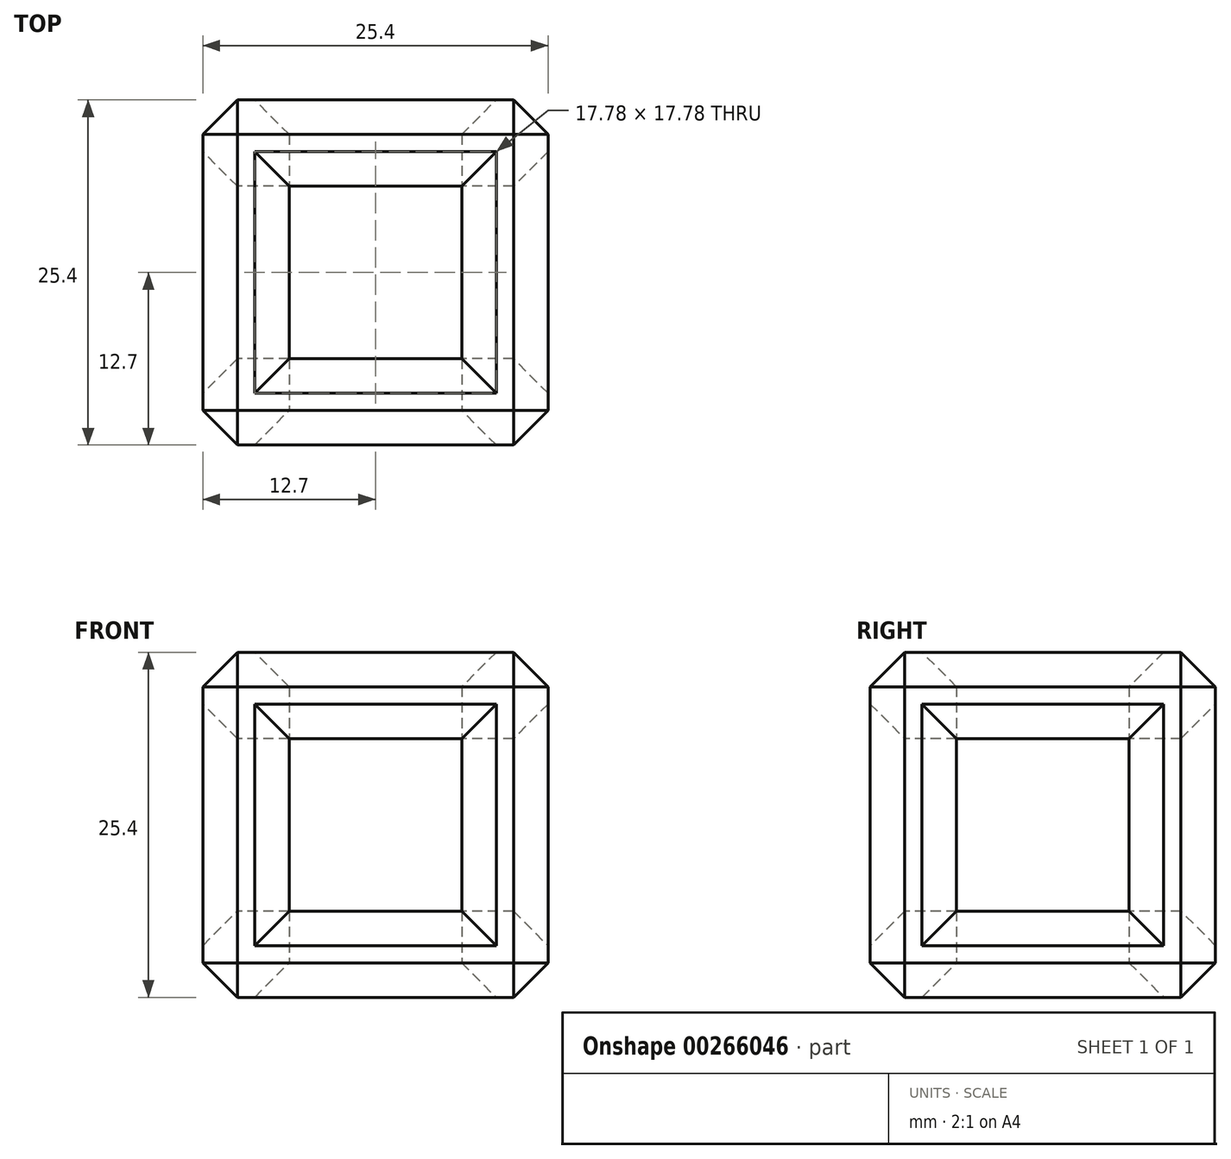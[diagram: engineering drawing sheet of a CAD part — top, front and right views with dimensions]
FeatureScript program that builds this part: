
annotation { "Feature Type Name" : "Feature", "Feature Type Description" : "" }
export const myFeature = defineFeature(function(context is Context, id is Id, definition is map)
    precondition{}
    {
        {
            var Q0;
            Q0=qCreatedBy(makeId("Top.planeOp"),FACE);
            var sketch = newSketch(context, id + "F0", { "sketchPlane" : qUnion([Q0])});
            skLineSegment(sketch, "E0.bottom", {"start": v(6.35, -6.35) * mm, "end": v(-6.35, -6.35) * mm});
            skLineSegment(sketch, "E0.top", {"start": v(6.35, 6.35) * mm, "end": v(-6.35, 6.35) * mm});
            skLineSegment(sketch, "E0.left", {"start": v(6.35, -6.35) * mm, "end": v(6.35, 6.35) * mm});
            skLineSegment(sketch, "E0.right", {"start": v(-6.35, -6.35) * mm, "end": v(-6.35, 6.35) * mm});
            skPoint(sketch, "E0.middle", {"position": v(0, 0) * mm});
            skLineSegment(sketch, "E1.bottom", {"start": v(12.7, -12.7) * mm, "end": v(-12.7, -12.7) * mm});
            skLineSegment(sketch, "E1.top", {"start": v(12.7, 12.7) * mm, "end": v(-12.7, 12.7) * mm});
            skLineSegment(sketch, "E1.left", {"start": v(12.7, -12.7) * mm, "end": v(12.7, 12.7) * mm});
            skLineSegment(sketch, "E1.right", {"start": v(-12.7, -12.7) * mm, "end": v(-12.7, 12.7) * mm});
            skSolve(sketch);
        }
        {
            var Q0;
            Q0=makeQuery(id+"F0.imprint","IMPRINT",FACE,{"disambiguationData":[TD([[makeQuery(id+"F0.imprint","IMPRINT",EDGE,{"derivedFrom":sQuery(id+"F0.wireOp",EDGE,"E0.bottom")}),1.0]])]});
            extrude(context, id + "F1", {"entities" : qUnion([Q0]), "depth" : 25.4 * mm, "offsetDistance" : 25.4 * mm});
        }
        {
            var Q0;
            Q0=qCreatedBy(makeId("Right.planeOp"),FACE);
            var sketch = newSketch(context, id + "F2", { "sketchPlane" : qUnion([Q0])});
            skLineSegment(sketch, "E2.bottom", {"start": v(-6.35, 6.35) * mm, "end": v(6.35, 6.35) * mm});
            skLineSegment(sketch, "E2.top", {"start": v(-6.35, 19.05) * mm, "end": v(6.35, 19.05) * mm});
            skLineSegment(sketch, "E2.left", {"start": v(-6.35, 6.35) * mm, "end": v(-6.35, 19.05) * mm});
            skLineSegment(sketch, "E2.right", {"start": v(6.35, 6.35) * mm, "end": v(6.35, 19.05) * mm});
            skPoint(sketch, "E2.middle", {"position": v(0, 12.7) * mm});
            skSolve(sketch);
        }
        {
            var Q0;
            Q0=qSketchRegion(id+"F2",true);
            extrude(context, id + "F3", {"entities" : qUnion([Q0]), "operationType" : NewBodyOperationType.REMOVE, "endBound" : BoundingType.SYMMETRIC, "depth" : 87.88 * mm, "offsetDistance" : 25.4 * mm});
        }
        {
            var Q0;
            Q0=qCreatedBy(makeId("Front.planeOp"),FACE);
            var sketch = newSketch(context, id + "F4", { "sketchPlane" : qUnion([Q0])});
            skLineSegment(sketch, "E3.bottom", {"start": v(-6.35, 6.35) * mm, "end": v(6.35, 6.35) * mm});
            skLineSegment(sketch, "E3.top", {"start": v(-6.35, 19.05) * mm, "end": v(6.35, 19.05) * mm});
            skLineSegment(sketch, "E3.left", {"start": v(-6.35, 6.35) * mm, "end": v(-6.35, 19.05) * mm});
            skLineSegment(sketch, "E3.right", {"start": v(6.35, 6.35) * mm, "end": v(6.35, 19.05) * mm});
            skPoint(sketch, "E3.middle", {"position": v(0, 12.7) * mm});
            skSolve(sketch);
        }
        {
            var Q0;
            Q0=makeQuery(id+"F4.imprint","IMPRINT",FACE,{"disambiguationData":[TD([[makeQuery(id+"F4.imprint","IMPRINT",EDGE,{"derivedFrom":sQuery(id+"F4.wireOp",EDGE,"E3.bottom")}),1.0]])]});
            extrude(context, id + "F5", {"entities" : qUnion([Q0]), "operationType" : NewBodyOperationType.REMOVE, "endBound" : BoundingType.SYMMETRIC, "oppositeDirection" : true, "depth" : 78.23 * mm});
        }
        {
            var Q0;
            Q0=makeQuery(id+"F1.opExtrude","CAP_EDGE",EDGE,{"disambiguationData":[OSD([sQuery(id+"F0.wireOp",EDGE,"E0.bottom")])],"isStart":true});
            var Q1;
            Q1=makeQuery(id+"F1.opExtrude","CAP_EDGE",EDGE,{"disambiguationData":[OSD([sQuery(id+"F0.wireOp",EDGE,"E0.right")])],"isStart":true});
            var Q2;
            Q2=makeQuery(id+"F1.opExtrude","CAP_EDGE",EDGE,{"disambiguationData":[OSD([sQuery(id+"F0.wireOp",EDGE,"E0.top")])],"isStart":true});
            var Q3;
            Q3=makeQuery(id+"F1.opExtrude","CAP_EDGE",EDGE,{"disambiguationData":[OSD([sQuery(id+"F0.wireOp",EDGE,"E0.left")])],"isStart":true});
            var Q4;
            Q4=makeQuery(id+"F3.boolean.opBoolean","INTERSECT",EDGE,{"derivedFrom":[makeQuery(id+"F1.opExtrude","SWEPT_FACE",FACE,{"disambiguationData":[OSD([sQuery(id+"F0.wireOp",EDGE,"E1.left")])]}),makeQuery(id+"F3.opExtrude","SWEPT_FACE",FACE,{"disambiguationData":[OSD([sQuery(id+"F2.wireOp",EDGE,"E2.right")])]})]});
            var Q5;
            Q5=makeQuery(id+"F3.boolean.opBoolean","INTERSECT",EDGE,{"derivedFrom":[makeQuery(id+"F1.opExtrude","SWEPT_FACE",FACE,{"disambiguationData":[OSD([sQuery(id+"F0.wireOp",EDGE,"E1.left")])]}),makeQuery(id+"F3.opExtrude","SWEPT_FACE",FACE,{"disambiguationData":[OSD([sQuery(id+"F2.wireOp",EDGE,"E2.top")])]})]});
            var Q6;
            Q6=makeQuery(id+"F3.boolean.opBoolean","INTERSECT",EDGE,{"derivedFrom":[makeQuery(id+"F1.opExtrude","SWEPT_FACE",FACE,{"disambiguationData":[OSD([sQuery(id+"F0.wireOp",EDGE,"E1.left")])]}),makeQuery(id+"F3.opExtrude","SWEPT_FACE",FACE,{"disambiguationData":[OSD([sQuery(id+"F2.wireOp",EDGE,"E2.left")])]})]});
            var Q7;
            Q7=makeQuery(id+"F3.boolean.opBoolean","INTERSECT",EDGE,{"derivedFrom":[makeQuery(id+"F1.opExtrude","SWEPT_FACE",FACE,{"disambiguationData":[OSD([sQuery(id+"F0.wireOp",EDGE,"E1.left")])]}),makeQuery(id+"F3.opExtrude","SWEPT_FACE",FACE,{"disambiguationData":[OSD([sQuery(id+"F2.wireOp",EDGE,"E2.bottom")])]})]});
            var Q8;
            Q8=makeQuery(id+"F3.boolean.opBoolean","INTERSECT",EDGE,{"derivedFrom":[makeQuery(id+"F1.opExtrude","SWEPT_FACE",FACE,{"disambiguationData":[OSD([sQuery(id+"F0.wireOp",EDGE,"E1.right")])]}),makeQuery(id+"F3.opExtrude","SWEPT_FACE",FACE,{"disambiguationData":[OSD([sQuery(id+"F2.wireOp",EDGE,"E2.left")])]})]});
            var Q9;
            Q9=makeQuery(id+"F3.boolean.opBoolean","INTERSECT",EDGE,{"derivedFrom":[makeQuery(id+"F1.opExtrude","SWEPT_FACE",FACE,{"disambiguationData":[OSD([sQuery(id+"F0.wireOp",EDGE,"E1.right")])]}),makeQuery(id+"F3.opExtrude","SWEPT_FACE",FACE,{"disambiguationData":[OSD([sQuery(id+"F2.wireOp",EDGE,"E2.top")])]})]});
            var Q10;
            Q10=makeQuery(id+"F3.boolean.opBoolean","INTERSECT",EDGE,{"derivedFrom":[makeQuery(id+"F1.opExtrude","SWEPT_FACE",FACE,{"disambiguationData":[OSD([sQuery(id+"F0.wireOp",EDGE,"E1.right")])]}),makeQuery(id+"F3.opExtrude","SWEPT_FACE",FACE,{"disambiguationData":[OSD([sQuery(id+"F2.wireOp",EDGE,"E2.bottom")])]})]});
            var Q11;
            Q11=makeQuery(id+"F3.boolean.opBoolean","INTERSECT",EDGE,{"derivedFrom":[makeQuery(id+"F1.opExtrude","SWEPT_FACE",FACE,{"disambiguationData":[OSD([sQuery(id+"F0.wireOp",EDGE,"E1.right")])]}),makeQuery(id+"F3.opExtrude","SWEPT_FACE",FACE,{"disambiguationData":[OSD([sQuery(id+"F2.wireOp",EDGE,"E2.right")])]})]});
            var Q12;
            Q12=makeQuery(id+"F1.opExtrude","CAP_EDGE",EDGE,{"disambiguationData":[OSD([sQuery(id+"F0.wireOp",EDGE,"E0.bottom")])],"isStart":false});
            var Q13;
            Q13=makeQuery(id+"F1.opExtrude","CAP_EDGE",EDGE,{"disambiguationData":[OSD([sQuery(id+"F0.wireOp",EDGE,"E0.right")])],"isStart":false});
            var Q14;
            Q14=makeQuery(id+"F1.opExtrude","CAP_EDGE",EDGE,{"disambiguationData":[OSD([sQuery(id+"F0.wireOp",EDGE,"E0.top")])],"isStart":false});
            var Q15;
            Q15=makeQuery(id+"F1.opExtrude","CAP_EDGE",EDGE,{"disambiguationData":[OSD([sQuery(id+"F0.wireOp",EDGE,"E0.left")])],"isStart":false});
            var Q16;
            Q16=makeQuery(id+"F5.boolean.opBoolean","INTERSECT",EDGE,{"derivedFrom":[makeQuery(id+"F1.opExtrude","SWEPT_FACE",FACE,{"disambiguationData":[OSD([sQuery(id+"F0.wireOp",EDGE,"E1.top")])]}),makeQuery(id+"F5.opExtrude","SWEPT_FACE",FACE,{"disambiguationData":[OSD([sQuery(id+"F4.wireOp",EDGE,"E3.right")])]})]});
            var Q17;
            Q17=makeQuery(id+"F5.boolean.opBoolean","INTERSECT",EDGE,{"derivedFrom":[makeQuery(id+"F1.opExtrude","SWEPT_FACE",FACE,{"disambiguationData":[OSD([sQuery(id+"F0.wireOp",EDGE,"E1.top")])]}),makeQuery(id+"F5.opExtrude","SWEPT_FACE",FACE,{"disambiguationData":[OSD([sQuery(id+"F4.wireOp",EDGE,"E3.top")])]})]});
            var Q18;
            Q18=makeQuery(id+"F5.boolean.opBoolean","INTERSECT",EDGE,{"derivedFrom":[makeQuery(id+"F1.opExtrude","SWEPT_FACE",FACE,{"disambiguationData":[OSD([sQuery(id+"F0.wireOp",EDGE,"E1.top")])]}),makeQuery(id+"F5.opExtrude","SWEPT_FACE",FACE,{"disambiguationData":[OSD([sQuery(id+"F4.wireOp",EDGE,"E3.bottom")])]})]});
            var Q19;
            Q19=makeQuery(id+"F5.boolean.opBoolean","INTERSECT",EDGE,{"derivedFrom":[makeQuery(id+"F1.opExtrude","SWEPT_FACE",FACE,{"disambiguationData":[OSD([sQuery(id+"F0.wireOp",EDGE,"E1.top")])]}),makeQuery(id+"F5.opExtrude","SWEPT_FACE",FACE,{"disambiguationData":[OSD([sQuery(id+"F4.wireOp",EDGE,"E3.left")])]})]});
            var Q20;
            Q20=makeQuery(id+"F5.boolean.opBoolean","INTERSECT",EDGE,{"derivedFrom":[makeQuery(id+"F1.opExtrude","SWEPT_FACE",FACE,{"disambiguationData":[OSD([sQuery(id+"F0.wireOp",EDGE,"E1.bottom")])]}),makeQuery(id+"F5.opExtrude","SWEPT_FACE",FACE,{"disambiguationData":[OSD([sQuery(id+"F4.wireOp",EDGE,"E3.top")])]})]});
            var Q21;
            Q21=makeQuery(id+"F5.boolean.opBoolean","INTERSECT",EDGE,{"derivedFrom":[makeQuery(id+"F1.opExtrude","SWEPT_FACE",FACE,{"disambiguationData":[OSD([sQuery(id+"F0.wireOp",EDGE,"E1.bottom")])]}),makeQuery(id+"F5.opExtrude","SWEPT_FACE",FACE,{"disambiguationData":[OSD([sQuery(id+"F4.wireOp",EDGE,"E3.right")])]})]});
            var Q22;
            Q22=makeQuery(id+"F5.boolean.opBoolean","INTERSECT",EDGE,{"derivedFrom":[makeQuery(id+"F1.opExtrude","SWEPT_FACE",FACE,{"disambiguationData":[OSD([sQuery(id+"F0.wireOp",EDGE,"E1.bottom")])]}),makeQuery(id+"F5.opExtrude","SWEPT_FACE",FACE,{"disambiguationData":[OSD([sQuery(id+"F4.wireOp",EDGE,"E3.bottom")])]})]});
            var Q23;
            Q23=makeQuery(id+"F5.boolean.opBoolean","INTERSECT",EDGE,{"derivedFrom":[makeQuery(id+"F1.opExtrude","SWEPT_FACE",FACE,{"disambiguationData":[OSD([sQuery(id+"F0.wireOp",EDGE,"E1.bottom")])]}),makeQuery(id+"F5.opExtrude","SWEPT_FACE",FACE,{"disambiguationData":[OSD([sQuery(id+"F4.wireOp",EDGE,"E3.left")])]})]});
            chamfer(context, id + "F6", {"entities" : qUnion([Q0, Q1, Q2, Q3, Q4, Q5, Q6, Q7, Q8, Q9, Q10, Q11, Q12, Q13, Q14, Q15, Q16, Q17, Q18, Q19, Q20, Q21, Q22, Q23]), "width" : 2.54 * mm, "tangentPropagation" : true});
        }
        {
            var Q0;
            Q0=makeQuery(id+"F1.opExtrude","CAP_EDGE",EDGE,{"disambiguationData":[OSD([sQuery(id+"F0.wireOp",EDGE,"E1.left")])],"isStart":true});
            var Q1;
            Q1=makeQuery(id+"F1.opExtrude","SWEPT_EDGE",EDGE,{"disambiguationData":[OSD([sQuery(id+"F0.wireOp",EDGE,"E1.bottom"),sQuery(id+"F0.wireOp",EDGE,"E1.left")])]});
            var Q2;
            Q2=makeQuery(id+"F1.opExtrude","CAP_EDGE",EDGE,{"disambiguationData":[OSD([sQuery(id+"F0.wireOp",EDGE,"E1.bottom")])],"isStart":true});
            var Q3;
            Q3=makeQuery(id+"F1.opExtrude","CAP_EDGE",EDGE,{"disambiguationData":[OSD([sQuery(id+"F0.wireOp",EDGE,"E1.bottom")])],"isStart":false});
            var Q4;
            Q4=makeQuery(id+"F1.opExtrude","SWEPT_EDGE",EDGE,{"disambiguationData":[OSD([sQuery(id+"F0.wireOp",EDGE,"E1.bottom"),sQuery(id+"F0.wireOp",EDGE,"E1.right")])]});
            var Q5;
            Q5=makeQuery(id+"F1.opExtrude","CAP_EDGE",EDGE,{"disambiguationData":[OSD([sQuery(id+"F0.wireOp",EDGE,"E1.right")])],"isStart":true});
            var Q6;
            Q6=makeQuery(id+"F1.opExtrude","CAP_EDGE",EDGE,{"disambiguationData":[OSD([sQuery(id+"F0.wireOp",EDGE,"E1.top")])],"isStart":true});
            var Q7;
            Q7=makeQuery(id+"F1.opExtrude","SWEPT_EDGE",EDGE,{"disambiguationData":[OSD([sQuery(id+"F0.wireOp",EDGE,"E1.top"),sQuery(id+"F0.wireOp",EDGE,"E1.left")])]});
            var Q8;
            Q8=makeQuery(id+"F1.opExtrude","CAP_EDGE",EDGE,{"disambiguationData":[OSD([sQuery(id+"F0.wireOp",EDGE,"E1.left")])],"isStart":false});
            var Q9;
            Q9=makeQuery(id+"F1.opExtrude","CAP_EDGE",EDGE,{"disambiguationData":[OSD([sQuery(id+"F0.wireOp",EDGE,"E1.top")])],"isStart":false});
            var Q10;
            Q10=makeQuery(id+"F1.opExtrude","CAP_EDGE",EDGE,{"disambiguationData":[OSD([sQuery(id+"F0.wireOp",EDGE,"E1.right")])],"isStart":false});
            var Q11;
            Q11=makeQuery(id+"F1.opExtrude","SWEPT_EDGE",EDGE,{"disambiguationData":[OSD([sQuery(id+"F0.wireOp",EDGE,"E1.top"),sQuery(id+"F0.wireOp",EDGE,"E1.right")])]});
            chamfer(context, id + "F7", {"entities" : qUnion([Q0, Q1, Q2, Q3, Q4, Q5, Q6, Q7, Q8, Q9, Q10, Q11]), "width" : 2.54 * mm, "tangentPropagation" : true});
        }
    });
